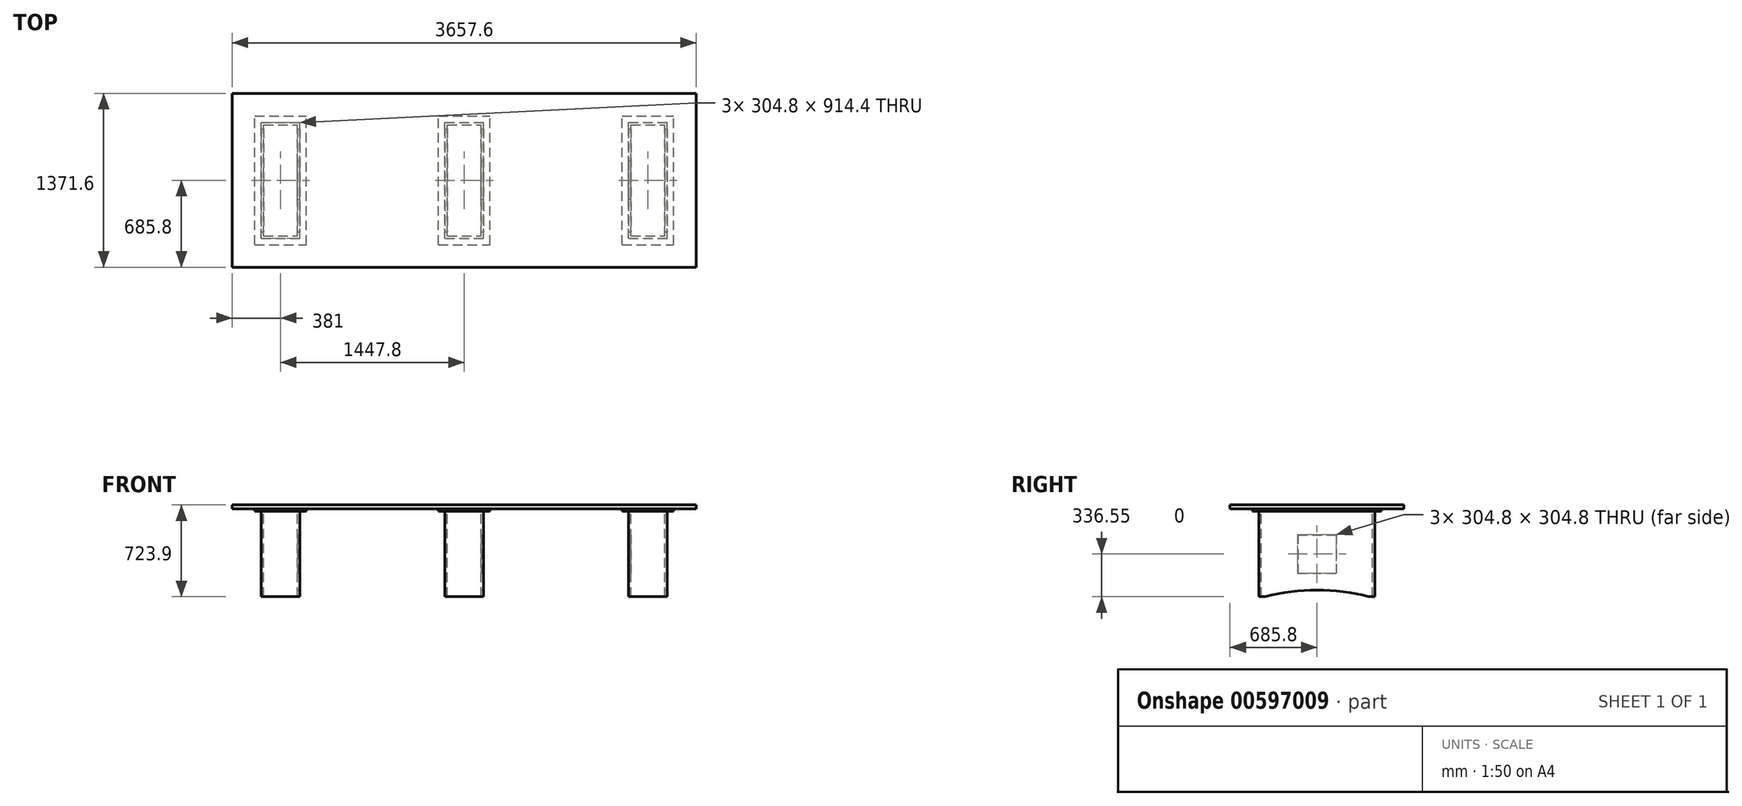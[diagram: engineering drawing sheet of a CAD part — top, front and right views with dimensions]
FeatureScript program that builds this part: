
annotation { "Feature Type Name" : "Feature", "Feature Type Description" : "" }
export const myFeature = defineFeature(function(context is Context, id is Id, definition is map)
    precondition{}
    {
        {
            var Q0;
            Q0=qCreatedBy(makeId("Top.planeOp"),FACE);
            var sketch = newSketch(context, id + "F0", { "sketchPlane" : qUnion([Q0])});
            skLineSegment(sketch, "E0.bottom", {"start": v(-1828.8, 685.8) * mm, "end": v(1828.8, 685.8) * mm});
            skLineSegment(sketch, "E0.top", {"start": v(-1828.8, -685.8) * mm, "end": v(1828.8, -685.8) * mm});
            skLineSegment(sketch, "E0.left", {"start": v(-1828.8, 685.8) * mm, "end": v(-1828.8, -685.8) * mm});
            skLineSegment(sketch, "E0.right", {"start": v(1828.8, 685.8) * mm, "end": v(1828.8, -685.8) * mm});
            skPoint(sketch, "E0.middle", {"position": v(0, 0) * mm});
            skSolve(sketch);
        }
        {
            var Q0;
            Q0 = qSketchRegion(id + "F0", true);
            extrude(context, id + "F1", {"entities" : qUnion([Q0]), "oppositeDirection" : true, "depth" : 31.75 * mm, "offsetDistance" : 25.4 * mm});
        }
        {
            var Q0;
            Q0=makeQuery(id+"F1.opExtrude","CAP_FACE",FACE,{"disambiguationData":[OSD([sQuery(id+"F0.wireOp",EDGE,"E0.bottom"),sQuery(id+"F0.wireOp",EDGE,"E0.top"),sQuery(id+"F0.wireOp",EDGE,"E0.left"),sQuery(id+"F0.wireOp",EDGE,"E0.right")])],"isStart":false});
            var sketch = newSketch(context, id + "F2", { "sketchPlane" : qUnion([Q0])});
            skLineSegment(sketch, "E1.bottom", {"start": v(-1651, 508) * mm, "end": v(-1244.6, 508) * mm});
            skLineSegment(sketch, "E1.top", {"start": v(-1651, -508) * mm, "end": v(-1244.6, -508) * mm});
            skLineSegment(sketch, "E1.left", {"start": v(-1651, 508) * mm, "end": v(-1651, -508) * mm});
            skLineSegment(sketch, "E1.right", {"start": v(-1244.6, 508) * mm, "end": v(-1244.6, -508) * mm});
            skLineSegment(sketch, "E2.bottom", {"start": v(-203.2, 508) * mm, "end": v(203.2, 508) * mm});
            skLineSegment(sketch, "E2.top", {"start": v(-203.2, -508) * mm, "end": v(203.2, -508) * mm});
            skLineSegment(sketch, "E2.left", {"start": v(-203.2, 508) * mm, "end": v(-203.2, -508) * mm});
            skLineSegment(sketch, "E2.right", {"start": v(203.2, 508) * mm, "end": v(203.2, -508) * mm});
            skPoint(sketch, "E2.middle", {"position": v(0, 0) * mm});
            skLineSegment(sketch, "E3.bottom", {"start": v(1244.6, 508) * mm, "end": v(1651, 508) * mm});
            skLineSegment(sketch, "E3.top", {"start": v(1244.6, -508) * mm, "end": v(1651, -508) * mm});
            skLineSegment(sketch, "E3.left", {"start": v(1244.6, 508) * mm, "end": v(1244.6, -508) * mm});
            skLineSegment(sketch, "E3.right", {"start": v(1651, 508) * mm, "end": v(1651, -508) * mm});
            skLineSegment(sketch, "E4.0", {"start": v(-1295.4, 457.2) * mm, "end": v(-1295.4, -457.2) * mm});
            skLineSegment(sketch, "E4.1", {"start": v(-1600.2, 457.2) * mm, "end": v(-1295.4, 457.2) * mm});
            skLineSegment(sketch, "E4.2", {"start": v(-1600.2, 457.2) * mm, "end": v(-1600.2, -457.2) * mm});
            skLineSegment(sketch, "E4.3", {"start": v(-1600.2, -457.2) * mm, "end": v(-1295.4, -457.2) * mm});
            skLineSegment(sketch, "E5.0", {"start": v(-152.4, 457.2) * mm, "end": v(-152.4, -457.2) * mm});
            skLineSegment(sketch, "E5.1", {"start": v(-152.4, 457.2) * mm, "end": v(152.4, 457.2) * mm});
            skLineSegment(sketch, "E5.2", {"start": v(152.4, 457.2) * mm, "end": v(152.4, -457.2) * mm});
            skLineSegment(sketch, "E5.3", {"start": v(-152.4, -457.2) * mm, "end": v(152.4, -457.2) * mm});
            skLineSegment(sketch, "E6.0", {"start": v(1295.4, 457.2) * mm, "end": v(1295.4, -457.2) * mm});
            skLineSegment(sketch, "E6.1", {"start": v(1295.4, 457.2) * mm, "end": v(1600.2, 457.2) * mm});
            skLineSegment(sketch, "E6.2", {"start": v(1600.2, 457.2) * mm, "end": v(1600.2, -457.2) * mm});
            skLineSegment(sketch, "E6.3", {"start": v(1295.4, -457.2) * mm, "end": v(1600.2, -457.2) * mm});
            skSolve(sketch);
        }
        {
            var Q0;
            Q0 = qSketchRegion(id + "F2", true);
            extrude(context, id + "F3", {"entities" : qUnion([Q0]), "flatOperationType" : FlatOperationType.REMOVE, "depth" : 19.05 * mm, "offsetDistance" : 25.4 * mm, "domain" : OperationDomain.MODEL});
        }
        {
            var Q0;
            Q0=makeQuery(id+"F3.opExtrude","CAP_FACE",FACE,{"disambiguationData":[OSD([sQuery(id+"F2.wireOp",EDGE,"E1.bottom"),sQuery(id+"F2.wireOp",EDGE,"E1.top"),sQuery(id+"F2.wireOp",EDGE,"E1.left"),sQuery(id+"F2.wireOp",EDGE,"E1.right"),sQuery(id+"F2.wireOp",EDGE,"E4.0"),sQuery(id+"F2.wireOp",EDGE,"E4.1"),sQuery(id+"F2.wireOp",EDGE,"E4.2"),sQuery(id+"F2.wireOp",EDGE,"E4.3")])],"isStart":false});
            var sketch = newSketch(context, id + "F4", { "sketchPlane" : qUnion([Q0])});
            skLineSegment(sketch, "E7.bottom", {"start": v(-1600.2, 457.2) * mm, "end": v(-1295.4, 457.2) * mm});
            skLineSegment(sketch, "E7.top", {"start": v(-1600.2, -457.2) * mm, "end": v(-1295.4, -457.2) * mm});
            skLineSegment(sketch, "E7.left", {"start": v(-1600.2, 457.2) * mm, "end": v(-1600.2, -457.2) * mm});
            skLineSegment(sketch, "E7.right", {"start": v(-1295.4, 457.2) * mm, "end": v(-1295.4, -457.2) * mm});
            skLineSegment(sketch, "E8.0", {"start": v(-152.4, 457.2) * mm, "end": v(-152.4, -457.2) * mm});
            skLineSegment(sketch, "E8.1", {"start": v(-152.4, 457.2) * mm, "end": v(152.4, 457.2) * mm});
            skLineSegment(sketch, "E8.2", {"start": v(152.4, 457.2) * mm, "end": v(152.4, -457.2) * mm});
            skLineSegment(sketch, "E8.3", {"start": v(-152.4, -457.2) * mm, "end": v(152.4, -457.2) * mm});
            skLineSegment(sketch, "E9.0", {"start": v(1295.4, 457.2) * mm, "end": v(1295.4, -457.2) * mm});
            skLineSegment(sketch, "E9.1", {"start": v(1295.4, 457.2) * mm, "end": v(1600.2, 457.2) * mm});
            skLineSegment(sketch, "E9.2", {"start": v(1600.2, 457.2) * mm, "end": v(1600.2, -457.2) * mm});
            skLineSegment(sketch, "E9.3", {"start": v(1295.4, -457.2) * mm, "end": v(1600.2, -457.2) * mm});
            skLineSegment(sketch, "E10.0", {"start": v(-1581.15, 438.15) * mm, "end": v(-1581.15, -438.15) * mm});
            skLineSegment(sketch, "E10.1", {"start": v(-1581.15, 438.15) * mm, "end": v(-1314.45, 438.15) * mm});
            skLineSegment(sketch, "E10.2", {"start": v(-1314.45, 438.15) * mm, "end": v(-1314.45, -438.15) * mm});
            skLineSegment(sketch, "E10.3", {"start": v(-1581.15, -438.15) * mm, "end": v(-1314.45, -438.15) * mm});
            skLineSegment(sketch, "E11.0", {"start": v(-133.35, 438.15) * mm, "end": v(-133.35, -438.15) * mm});
            skLineSegment(sketch, "E11.1", {"start": v(-133.35, 438.15) * mm, "end": v(133.35, 438.15) * mm});
            skLineSegment(sketch, "E11.2", {"start": v(133.35, 438.15) * mm, "end": v(133.35, -438.15) * mm});
            skLineSegment(sketch, "E11.3", {"start": v(-133.35, -438.15) * mm, "end": v(133.35, -438.15) * mm});
            skLineSegment(sketch, "E12.0", {"start": v(1314.45, 438.15) * mm, "end": v(1314.45, -438.15) * mm});
            skLineSegment(sketch, "E12.1", {"start": v(1314.45, 438.15) * mm, "end": v(1581.15, 438.15) * mm});
            skLineSegment(sketch, "E12.2", {"start": v(1581.15, 438.15) * mm, "end": v(1581.15, -438.15) * mm});
            skLineSegment(sketch, "E12.3", {"start": v(1314.45, -438.15) * mm, "end": v(1581.15, -438.15) * mm});
            skSolve(sketch);
        }
        {
            var Q0;
            Q0 = qSketchRegion(id + "F4", true);
            extrude(context, id + "F5", {"entities" : qUnion([Q0]), "depth" : 673.1 * mm, "offsetDistance" : 25.4 * mm});
        }
        {
            var Q0;
            Q0=makeQuery(id+"F5.opExtrude","SWEPT_FACE",FACE,{"disambiguationData":[OSD([sQuery(id+"F4.wireOp",EDGE,"E9.2")])]});
            var sketch = newSketch(context, id + "F6", { "sketchPlane" : qUnion([Q0])});
            skArc(sketch, "E13", {"start": v(406.4, -723.9) * mm, "mid": v(0, -673.1) * mm, "end": v(-406.4, -723.9) * mm});
            skLineSegment(sketch, "E14", {"start": v(-406.4, -723.9) * mm, "end": v(406.4, -723.9) * mm});
            skSolve(sketch);
        }
        {
            var Q0;
            Q0 = qSketchRegion(id + "F6", true);
            extrude(context, id + "F7", {"entities" : qUnion([Q0]), "operationType" : NewBodyOperationType.REMOVE, "oppositeDirection" : true, "depth" : 3657.6 * mm, "offsetDistance" : 25.4 * mm});
        }
        {
            var Q0;
            Q0=makeQuery(id+"F5.opExtrude","SWEPT_FACE",FACE,{"disambiguationData":[OSD([sQuery(id+"F4.wireOp",EDGE,"E8.2")])]});
            var sketch = newSketch(context, id + "F8", { "sketchPlane" : qUnion([Q0])});
            skArc(sketch, "E15.0", {"start": v(406.4, -723.9) * mm, "mid": v(0, -673.1) * mm, "end": v(-406.4, -723.9) * mm});
            skLineSegment(sketch, "E15.1", {"start": v(-457.2, -723.9) * mm, "end": v(457.2, -723.9) * mm});
            skSolve(sketch);
        }
        {
            var Q0;
            Q0 = qSketchRegion(id + "F8", true);
            extrude(context, id + "F9", {"entities" : qUnion([Q0]), "operationType" : NewBodyOperationType.REMOVE, "endBound" : BoundingType.THROUGH_ALL, "oppositeDirection" : true, "depth" : 25.4 * mm, "offsetDistance" : 25.4 * mm});
        }
        {
            var Q0;
            Q0=makeQuery(id+"F5.opExtrude","SWEPT_FACE",FACE,{"disambiguationData":[OSD([sQuery(id+"F4.wireOp",EDGE,"E7.right")])]});
            var sketch = newSketch(context, id + "F10", { "sketchPlane" : qUnion([Q0])});
            skLineSegment(sketch, "E16.bottom", {"start": v(-152.4, -234.95) * mm, "end": v(152.4, -234.95) * mm});
            skLineSegment(sketch, "E16.top", {"start": v(-152.4, -539.75) * mm, "end": v(152.4, -539.75) * mm});
            skLineSegment(sketch, "E16.left", {"start": v(-152.4, -234.95) * mm, "end": v(-152.4, -539.75) * mm});
            skLineSegment(sketch, "E16.right", {"start": v(152.4, -234.95) * mm, "end": v(152.4, -539.75) * mm});
            skPoint(sketch, "E16.middle", {"position": v(0, -387.35) * mm});
            skPoint(sketch, "E16.middle.positionSnap0", {"position": v(-457.2, -387.35) * mm});
            skPoint(sketch, "E16.centerSnap0", {"position": v(-457.2, -387.35) * mm});
            skSolve(sketch);
        }
        {
            var Q0;
            Q0 = qSketchRegion(id + "F10", true);
            extrude(context, id + "F11", {"entities" : qUnion([Q0]), "operationType" : NewBodyOperationType.REMOVE, "oppositeDirection" : true, "depth" : 25.4 * mm, "offsetDistance" : 25.4 * mm});
        }
        {
            var Q0;
            Q0=makeQuery(id+"F5.opExtrude","SWEPT_FACE",FACE,{"disambiguationData":[OSD([sQuery(id+"F4.wireOp",EDGE,"E8.2")])]});
            var sketch = newSketch(context, id + "F12", { "sketchPlane" : qUnion([Q0])});
            skLineSegment(sketch, "E17.bottom", {"start": v(-152.4, -234.95) * mm, "end": v(152.4, -234.95) * mm});
            skLineSegment(sketch, "E17.top", {"start": v(-152.4, -539.75) * mm, "end": v(152.4, -539.75) * mm});
            skLineSegment(sketch, "E17.left", {"start": v(-152.4, -234.95) * mm, "end": v(-152.4, -539.75) * mm});
            skLineSegment(sketch, "E17.right", {"start": v(152.4, -234.95) * mm, "end": v(152.4, -539.75) * mm});
            skPoint(sketch, "E17.middle", {"position": v(0, -387.35) * mm});
            skPoint(sketch, "E17.middle.positionSnap0", {"position": v(-457.2, -387.35) * mm});
            skPoint(sketch, "E17.middle.positionSnap1", {"position": v(0, -50.8) * mm});
            skPoint(sketch, "E17.centerSnap0", {"position": v(-457.2, -387.35) * mm});
            skPoint(sketch, "E17.centerSnap1", {"position": v(0, -50.8) * mm});
            skSolve(sketch);
        }
        {
            var Q0;
            Q0 = qSketchRegion(id + "F12", true);
            extrude(context, id + "F13", {"entities" : qUnion([Q0]), "operationType" : NewBodyOperationType.REMOVE, "oppositeDirection" : true, "depth" : 25.4 * mm, "offsetDistance" : 25.4 * mm});
        }
        {
            var Q0;
            Q0=makeQuery(id+"F5.opExtrude","SWEPT_FACE",FACE,{"disambiguationData":[OSD([sQuery(id+"F4.wireOp",EDGE,"E9.0")])]});
            var sketch = newSketch(context, id + "F14", { "sketchPlane" : qUnion([Q0])});
            skLineSegment(sketch, "E18.bottom", {"start": v(-152.4, -234.95) * mm, "end": v(152.4, -234.95) * mm});
            skLineSegment(sketch, "E18.top", {"start": v(-152.4, -539.75) * mm, "end": v(152.4, -539.75) * mm});
            skLineSegment(sketch, "E18.left", {"start": v(-152.4, -234.95) * mm, "end": v(-152.4, -539.75) * mm});
            skLineSegment(sketch, "E18.right", {"start": v(152.4, -234.95) * mm, "end": v(152.4, -539.75) * mm});
            skPoint(sketch, "E18.middle", {"position": v(0, -387.35) * mm});
            skPoint(sketch, "E18.middle.positionSnap0", {"position": v(-457.2, -387.35) * mm});
            skPoint(sketch, "E18.middle.positionSnap1", {"position": v(0, -50.8) * mm});
            skPoint(sketch, "E18.centerSnap0", {"position": v(-457.2, -387.35) * mm});
            skPoint(sketch, "E18.centerSnap1", {"position": v(0, -50.8) * mm});
            skSolve(sketch);
        }
        {
            var Q0;
            Q0 = qSketchRegion(id + "F14", true);
            extrude(context, id + "F15", {"entities" : qUnion([Q0]), "operationType" : NewBodyOperationType.REMOVE, "oppositeDirection" : true, "depth" : 25.4 * mm, "offsetDistance" : 25.4 * mm});
        }
        {
            var Q0;
            Q0=makeQuery(id+"F5.opExtrude","SWEPT_FACE",FACE,{"disambiguationData":[OSD([sQuery(id+"F4.wireOp",EDGE,"E7.right")])]});
            var sketch = newSketch(context, id + "F16", { "sketchPlane" : qUnion([Q0])});
            skLineSegment(sketch, "E19.bottom", {"start": v(-150.81, -236.54) * mm, "end": v(150.81, -236.54) * mm});
            skLineSegment(sketch, "E19.top", {"start": v(-150.81, -538.16) * mm, "end": v(150.81, -538.16) * mm});
            skLineSegment(sketch, "E19.left", {"start": v(-150.81, -236.54) * mm, "end": v(-150.81, -538.16) * mm});
            skLineSegment(sketch, "E19.right", {"start": v(150.81, -236.54) * mm, "end": v(150.81, -538.16) * mm});
            skPoint(sketch, "E19.middle", {"position": v(0, -387.35) * mm});
            skPoint(sketch, "E19.middle.positionSnap0", {"position": v(-457.2, -387.35) * mm});
            skPoint(sketch, "E19.middle.positionSnap1", {"position": v(0, -50.8) * mm});
            skPoint(sketch, "E19.centerSnap0", {"position": v(-457.2, -387.35) * mm});
            skPoint(sketch, "E19.centerSnap1", {"position": v(0, -50.8) * mm});
            skSolve(sketch);
        }
        {
            var Q0;
            Q0 = qSketchRegion(id + "F16", true);
            extrude(context, id + "F17", {"entities" : qUnion([Q0]), "oppositeDirection" : true, "depth" : 19.05 * mm, "offsetDistance" : 25.4 * mm});
        }
        {
            var Q0;
            Q0=makeQuery(id+"F5.opExtrude","SWEPT_FACE",FACE,{"disambiguationData":[OSD([sQuery(id+"F4.wireOp",EDGE,"E8.2")])]});
            var sketch = newSketch(context, id + "F18", { "sketchPlane" : qUnion([Q0])});
            skLineSegment(sketch, "E20.bottom", {"start": v(-150.81, -236.54) * mm, "end": v(150.81, -236.54) * mm});
            skLineSegment(sketch, "E20.top", {"start": v(-150.81, -538.16) * mm, "end": v(150.81, -538.16) * mm});
            skLineSegment(sketch, "E20.left", {"start": v(-150.81, -236.54) * mm, "end": v(-150.81, -538.16) * mm});
            skLineSegment(sketch, "E20.right", {"start": v(150.81, -236.54) * mm, "end": v(150.81, -538.16) * mm});
            skPoint(sketch, "E20.middle", {"position": v(0, -387.35) * mm});
            skPoint(sketch, "E20.middle.positionSnap0", {"position": v(-457.2, -387.35) * mm});
            skPoint(sketch, "E20.middle.positionSnap1", {"position": v(0, -50.8) * mm});
            skPoint(sketch, "E20.centerSnap0", {"position": v(-457.2, -387.35) * mm});
            skPoint(sketch, "E20.centerSnap1", {"position": v(0, -50.8) * mm});
            skSolve(sketch);
        }
        {
            var Q0;
            Q0 = qSketchRegion(id + "F18", true);
            extrude(context, id + "F19", {"entities" : qUnion([Q0]), "oppositeDirection" : true, "depth" : 19.05 * mm, "offsetDistance" : 25.4 * mm});
        }
        {
            var Q0;
            Q0=makeQuery(id+"F5.opExtrude","SWEPT_FACE",FACE,{"disambiguationData":[OSD([sQuery(id+"F4.wireOp",EDGE,"E9.0")])]});
            var sketch = newSketch(context, id + "F20", { "sketchPlane" : qUnion([Q0])});
            skLineSegment(sketch, "E21.bottom", {"start": v(150.81, -236.54) * mm, "end": v(-150.81, -236.54) * mm});
            skLineSegment(sketch, "E21.top", {"start": v(150.81, -538.16) * mm, "end": v(-150.81, -538.16) * mm});
            skLineSegment(sketch, "E21.left", {"start": v(150.81, -236.54) * mm, "end": v(150.81, -538.16) * mm});
            skLineSegment(sketch, "E21.right", {"start": v(-150.81, -236.54) * mm, "end": v(-150.81, -538.16) * mm});
            skPoint(sketch, "E21.middle", {"position": v(0, -387.35) * mm});
            skPoint(sketch, "E21.middle.positionSnap0", {"position": v(0, -50.8) * mm});
            skPoint(sketch, "E21.middle.positionSnap1", {"position": v(-152.4, -387.35) * mm});
            skPoint(sketch, "E21.centerSnap0", {"position": v(0, -50.8) * mm});
            skPoint(sketch, "E21.centerSnap1", {"position": v(-152.4, -387.35) * mm});
            skSolve(sketch);
        }
        {
            var Q0;
            Q0 = qSketchRegion(id + "F20", true);
            extrude(context, id + "F21", {"entities" : qUnion([Q0]), "oppositeDirection" : true, "depth" : 19.05 * mm, "offsetDistance" : 25.4 * mm});
        }
    });
